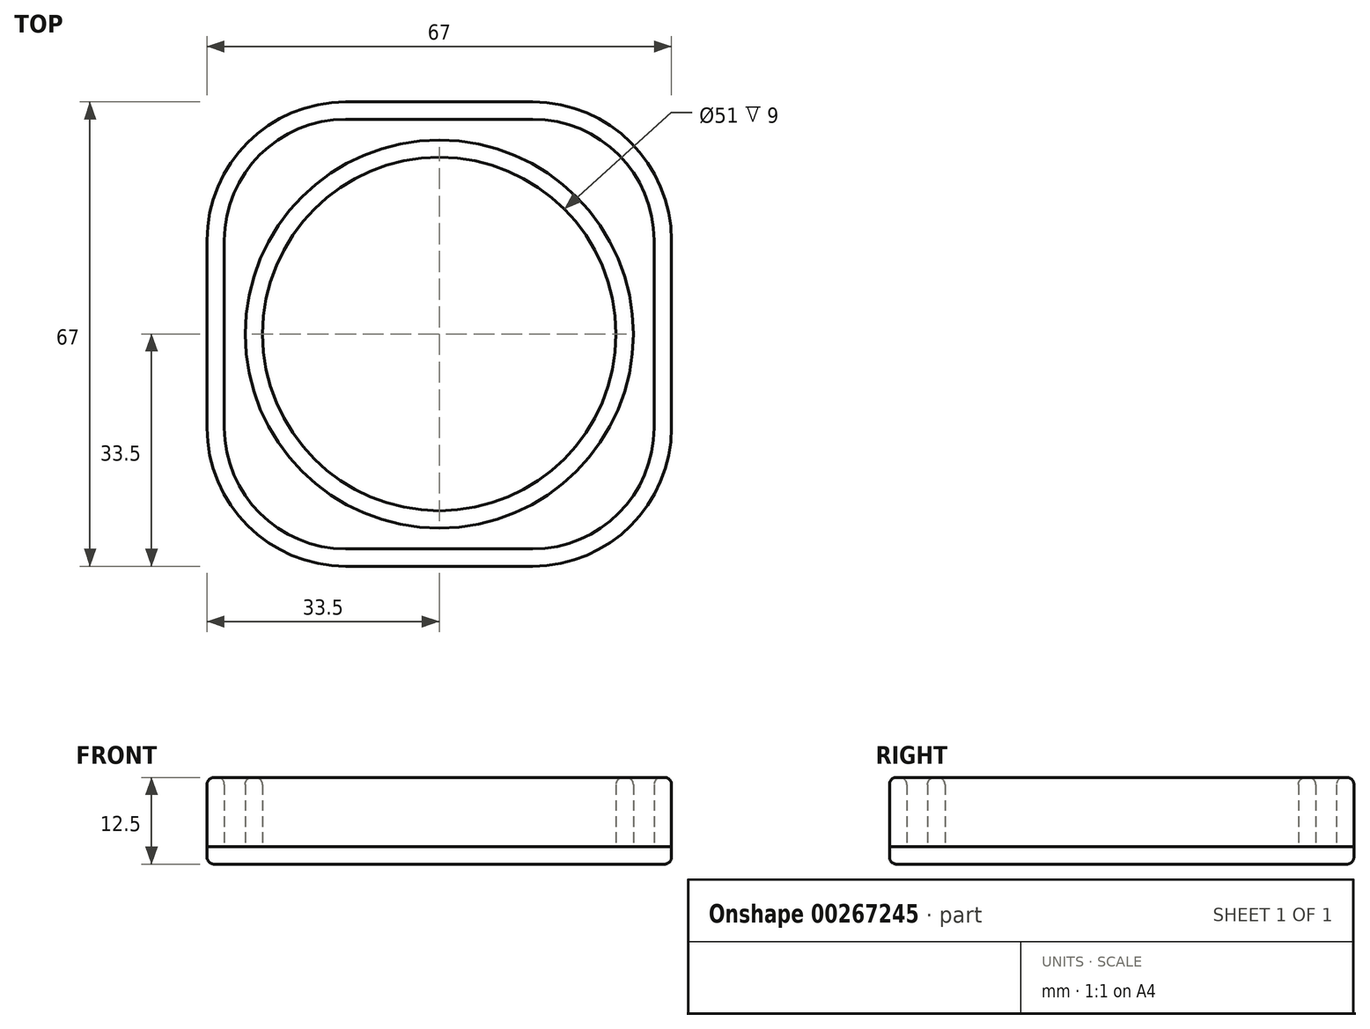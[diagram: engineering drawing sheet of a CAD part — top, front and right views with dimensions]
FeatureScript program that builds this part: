
annotation { "Feature Type Name" : "Feature", "Feature Type Description" : "" }
export const myFeature = defineFeature(function(context is Context, id is Id, definition is map)
    precondition{}
    {
        {
            var Q0;
            Q0=qCreatedBy(makeId("Top.planeOp"),FACE);
            var sketch = newSketch(context, id + "F0", { "sketchPlane" : qUnion([Q0])});
            skLineSegment(sketch, "E0.bottom", {"start": v(13.5, -33.5) * mm, "end": v(-13.5, -33.5) * mm});
            skLineSegment(sketch, "E0.top", {"start": v(13.5, 33.5) * mm, "end": v(-13.5, 33.5) * mm});
            skLineSegment(sketch, "E0.left", {"start": v(33.5, -13.5) * mm, "end": v(33.5, 13.5) * mm});
            skLineSegment(sketch, "E0.right", {"start": v(-33.5, -13.5) * mm, "end": v(-33.5, 13.5) * mm});
            skPoint(sketch, "E0.middle", {"position": v(0, 0) * mm});
            skCircle(sketch, "E1", {"center": v(0, 0) * mm, "radius": 25.5 * mm});
            skCircle(sketch, "E2.0", {"center": v(0, 0) * mm, "radius": 28 * mm});
            skPoint(sketch, "E3.visualSharp", {"position": v(-33.5, 33.5) * mm});
            skArc(sketch, "E3.filletArc", {"start": v(-13.5, 33.5) * mm, "mid": v(-27.64, 27.64) * mm, "end": v(-33.5, 13.5) * mm});
            skPoint(sketch, "E4.visualSharp", {"position": v(33.5, 33.5) * mm});
            skArc(sketch, "E4.filletArc", {"start": v(33.5, 13.5) * mm, "mid": v(27.64, 27.64) * mm, "end": v(13.5, 33.5) * mm});
            skPoint(sketch, "E5.visualSharp", {"position": v(33.5, -33.5) * mm});
            skArc(sketch, "E5.filletArc", {"start": v(13.5, -33.5) * mm, "mid": v(27.64, -27.64) * mm, "end": v(33.5, -13.5) * mm});
            skPoint(sketch, "E6.visualSharp", {"position": v(-33.5, -33.5) * mm});
            skArc(sketch, "E6.filletArc", {"start": v(-33.5, -13.5) * mm, "mid": v(-27.64, -27.64) * mm, "end": v(-13.5, -33.5) * mm});
            skLineSegment(sketch, "E7.0", {"start": v(13.5, -31) * mm, "end": v(-13.5, -31) * mm});
            skArc(sketch, "E7.1", {"start": v(-31, -13.5) * mm, "mid": v(-25.87, -25.87) * mm, "end": v(-13.5, -31) * mm});
            skArc(sketch, "E7.2", {"start": v(13.5, -31) * mm, "mid": v(25.87, -25.87) * mm, "end": v(31, -13.5) * mm});
            skLineSegment(sketch, "E7.3", {"start": v(-31, -13.5) * mm, "end": v(-31, 13.5) * mm});
            skLineSegment(sketch, "E7.4", {"start": v(31, -13.5) * mm, "end": v(31, 13.5) * mm});
            skArc(sketch, "E7.5", {"start": v(31, 13.5) * mm, "mid": v(25.87, 25.87) * mm, "end": v(13.5, 31) * mm});
            skLineSegment(sketch, "E7.6", {"start": v(13.5, 31) * mm, "end": v(-13.5, 31) * mm});
            skArc(sketch, "E7.7", {"start": v(-13.5, 31) * mm, "mid": v(-25.87, 25.87) * mm, "end": v(-31, 13.5) * mm});
            skLineSegment(sketch, "E8", {"start": v(-33.5, -15.08) * mm, "end": v(33.5, -15.08) * mm, "construction": true});
            skSolve(sketch);
        }
        {
            var Q0;
            Q0=makeQuery(id+"F0.imprint","IMPRINT",FACE,{"disambiguationData":[TD([[makeQuery(id+"F0.imprint","IMPRINT",EDGE,{"derivedFrom":sQuery(id+"F0.wireOp",EDGE,"E2.0")}),-1.0]])]});
            var Q1;
            Q1=makeQuery(id+"F0.imprint","IMPRINT",FACE,{"disambiguationData":[TD([[makeQuery(id+"F0.imprint","IMPRINT",EDGE,{"derivedFrom":sQuery(id+"F0.wireOp",EDGE,"E0.bottom")}),-1.0]])]});
            var Q2;
            Q2=makeQuery(id+"F0.imprint","IMPRINT",FACE,{"disambiguationData":[TD([[makeQuery(id+"F0.imprint","IMPRINT",EDGE,{"derivedFrom":sQuery(id+"F0.wireOp",EDGE,"E1")}),1.0]])]});
            var Q3;
            Q3=makeQuery(id+"F0.imprint","IMPRINT",FACE,{"disambiguationData":[TD([[makeQuery(id+"F0.imprint","IMPRINT",EDGE,{"derivedFrom":sQuery(id+"F0.wireOp",EDGE,"E1")}),-1.0]])]});
            extrude(context, id + "F1", {"entities" : qUnion([Q0, Q1, Q2, Q3]), "oppositeDirection" : true, "depth" : 2.5 * mm});
        }
        {
            var Q0;
            Q0=makeQuery(id+"F0.imprint","IMPRINT",FACE,{"disambiguationData":[TD([[makeQuery(id+"F0.imprint","IMPRINT",EDGE,{"derivedFrom":sQuery(id+"F0.wireOp",EDGE,"E1")}),-1.0]])]});
            var Q1;
            Q1=makeQuery(id+"F0.imprint","IMPRINT",FACE,{"disambiguationData":[TD([[makeQuery(id+"F0.imprint","IMPRINT",EDGE,{"derivedFrom":sQuery(id+"F0.wireOp",EDGE,"E0.bottom")}),-1.0]])]});
            extrude(context, id + "F2", {"entities" : qUnion([Q0, Q1]), "depth" : 10 * mm});
        }
        {
            var Q0;
            Q0=makeQuery(id+"F2.opExtrude","CAP_EDGE",EDGE,{"disambiguationData":[OSD([sQuery(id+"F0.wireOp",EDGE,"E1")])],"isStart":false});
            var Q1;
            Q1=makeQuery(id+"F2.opExtrude","CAP_EDGE",EDGE,{"disambiguationData":[OSD([sQuery(id+"F0.wireOp",EDGE,"E2.0")])],"isStart":false});
            fillet(context, id + "F3", {"entities" : qUnion([Q0, Q1]), "radius" : 1 * mm, "tangentPropagation" : true, "allowEdgeOverflow" : false});
        }
        {
            var Q0;
            Q0=makeQuery(id+"F2.opExtrude","CAP_FACE",FACE,{"disambiguationData":[OSD([sQuery(id+"F0.wireOp",EDGE,"E0.bottom"),sQuery(id+"F0.wireOp",EDGE,"E0.top"),sQuery(id+"F0.wireOp",EDGE,"E0.left"),sQuery(id+"F0.wireOp",EDGE,"E0.right"),sQuery(id+"F0.wireOp",EDGE,"E3.filletArc"),sQuery(id+"F0.wireOp",EDGE,"E4.filletArc"),sQuery(id+"F0.wireOp",EDGE,"E5.filletArc"),sQuery(id+"F0.wireOp",EDGE,"E6.filletArc"),sQuery(id+"F0.wireOp",EDGE,"E7.0"),sQuery(id+"F0.wireOp",EDGE,"E7.1"),sQuery(id+"F0.wireOp",EDGE,"E7.2"),sQuery(id+"F0.wireOp",EDGE,"E7.3"),sQuery(id+"F0.wireOp",EDGE,"E7.4"),sQuery(id+"F0.wireOp",EDGE,"E7.5"),sQuery(id+"F0.wireOp",EDGE,"E7.6"),sQuery(id+"F0.wireOp",EDGE,"E7.7")])],"isStart":false});
            var Q1;
            Q1=makeQuery(id+"F1.opExtrude","CAP_FACE",FACE,{"disambiguationData":[OSD([sQuery(id+"F0.wireOp",EDGE,"E0.bottom"),sQuery(id+"F0.wireOp",EDGE,"E0.top"),sQuery(id+"F0.wireOp",EDGE,"E0.left"),sQuery(id+"F0.wireOp",EDGE,"E0.right"),sQuery(id+"F0.wireOp",EDGE,"E3.filletArc"),sQuery(id+"F0.wireOp",EDGE,"E4.filletArc"),sQuery(id+"F0.wireOp",EDGE,"E5.filletArc"),sQuery(id+"F0.wireOp",EDGE,"E6.filletArc")])],"isStart":false});
            fillet(context, id + "F4", {"entities" : qUnion([Q0, Q1]), "radius" : 1 * mm, "tangentPropagation" : true, "allowEdgeOverflow" : false});
        }
    });
